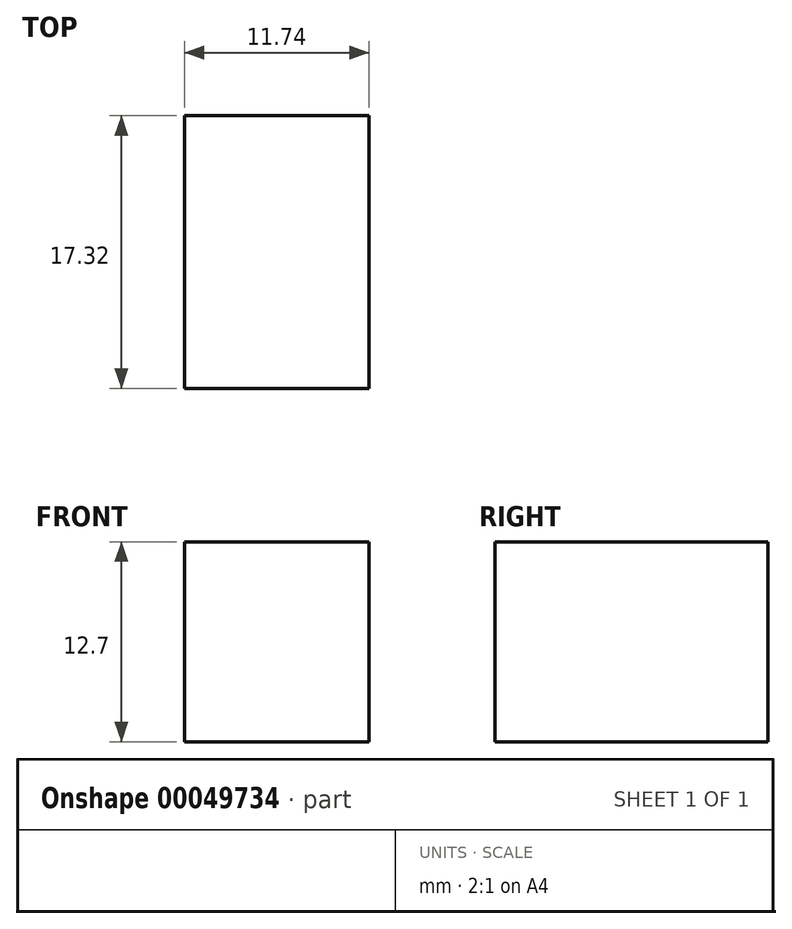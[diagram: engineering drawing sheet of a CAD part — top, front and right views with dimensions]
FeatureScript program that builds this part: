
annotation { "Feature Type Name" : "Feature", "Feature Type Description" : "" }
export const myFeature = defineFeature(function(context is Context, id is Id, definition is map)
    precondition{}
    {
        {
            var Q0;
            Q0=qCreatedBy(makeId("Top.planeOp"),FACE);
            var sketch = newSketch(context, id + "F0", { "sketchPlane" : qUnion([Q0])});
            skLineSegment(sketch, "E0.rect.bottom", {"start": v(-5.87, 8.66) * mm, "end": v(5.87, 8.66) * mm});
            skLineSegment(sketch, "E0.rect.top", {"start": v(-5.87, -8.66) * mm, "end": v(5.87, -8.66) * mm});
            skLineSegment(sketch, "E0.rect.left", {"start": v(-5.87, 8.66) * mm, "end": v(-5.87, -8.66) * mm});
            skLineSegment(sketch, "E0.rect.right", {"start": v(5.87, 8.66) * mm, "end": v(5.87, -8.66) * mm});
            skPoint(sketch, "E0.rect.middle", {"position": v(0, 0) * mm});
            skSolve(sketch);
        }
        {
            var Q0;
            Q0=makeQuery(id+"F0.imprint","IMPRINT",FACE,{"disambiguationData":[TD([[makeQuery(id+"F0.imprint","IMPRINT",EDGE,{"derivedFrom":sQuery(id+"F0.wireOp",EDGE,"E0.rect.bottom")}),-1.0]])]});
            extrude(context, id + "F1", {"entities" : qUnion([Q0]), "depth" : 12.7 * mm, "symmetric" : true});
        }
    });
